# Revit family: QF_Turbo Air_TGF-47SD5710d0bc-e6e3-4ae6-a539-0df53f637e5d
name_source: partatom
category: Specialty Equipment
revit_build: Autodesk Revit MEP 2012 (Build: 20110916_2132(x64)
units: mm (PartAtom-declared; Revit-internal decimal feet)

## types (3) — shared parameters
Apparent Power = 1346 VA
Assembly Code = E1090320
CSI MasterFormat = 11 41 13
Conn Plug = NEMA 5-20P
Cycle = 60 Hz
Depth = 2' - 7 7/16"
Description = Freezer Merchandiser
FL Amps = 12 A
Foodservice Equipment Identifier = Yes
HP = 1.25
Manufacturer = Turbo Air
Phase = 1
URL = www.turboairinc.com
Volts = 115 V
Weight in Pounds = 590
Width = 4' - 3 1/8"

## per-type parameters (varying)
| type | Body Material | Door Material | Lower Cowl Frame Material | Lower Door Frame Material | Model |
| Black | QF_Finishes_Black | QF_Finishes_Black | QF_Finishes_Black | QF_Finishes_Black | TGF-47SDB |
| White | QF_Finishes_White | QF_Finishes_White | QF_Finishes_White | QF_Finishes_White | TGF-47SDW |
| White - Wine | QF_Finishes_White | QF_Finishes_Anodized - Red | QF_Finishes_Anodized - Red | QF_Finishes_White | TGF-47SDV |

## geometry (parser evidence)
native form markers: Blend x19, Sweep x5
no freeform markers — native parametric forms only
